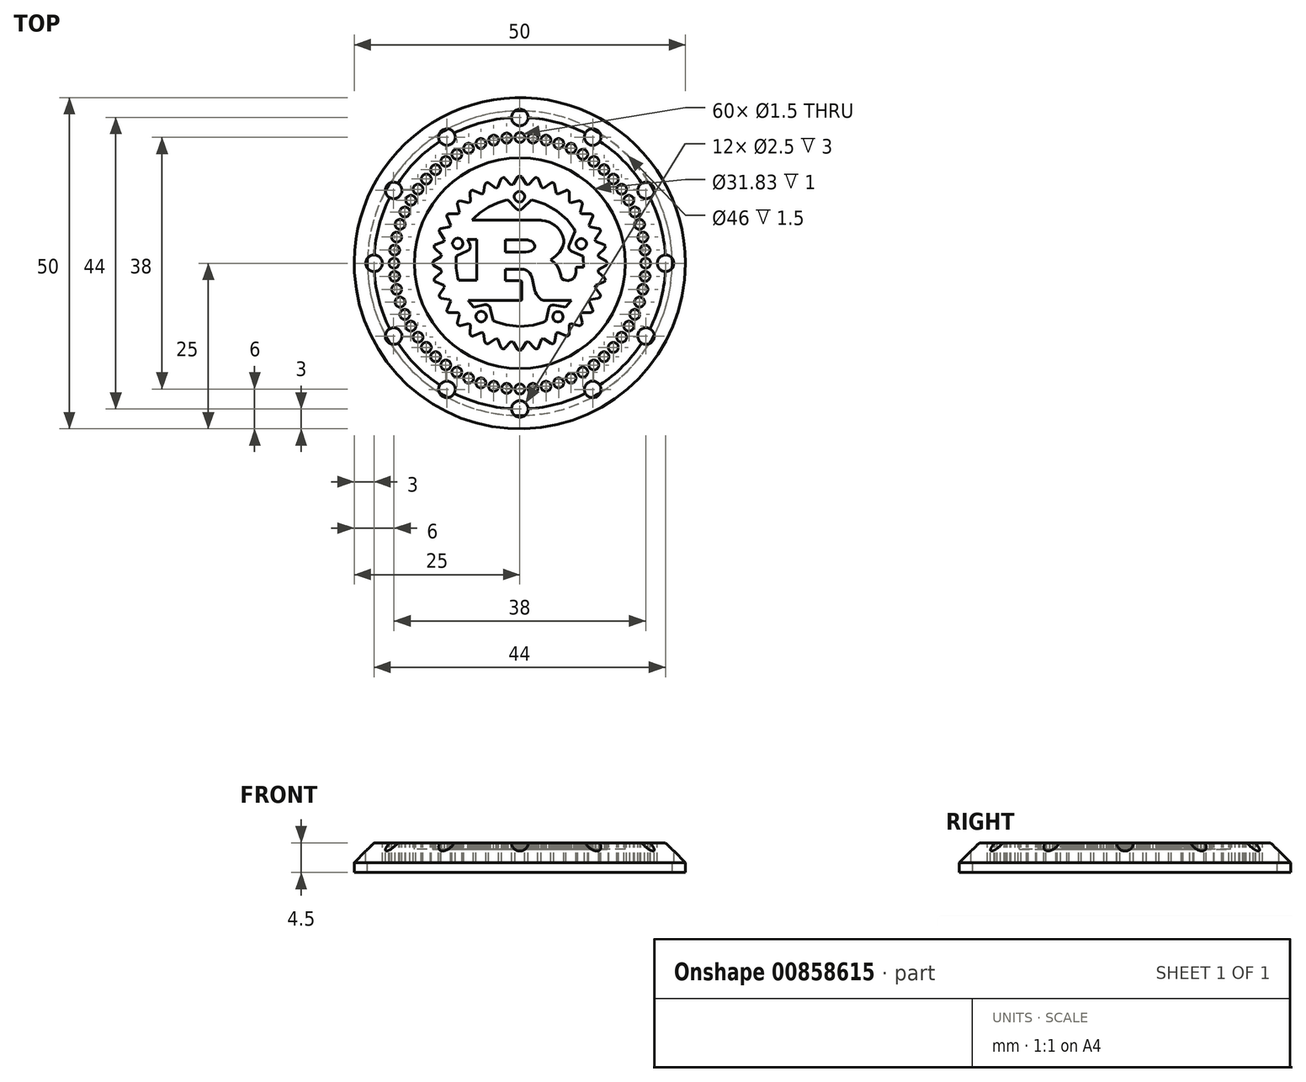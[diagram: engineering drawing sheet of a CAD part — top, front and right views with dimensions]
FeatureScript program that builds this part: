
annotation { "Feature Type Name" : "Feature", "Feature Type Description" : "" }
export const myFeature = defineFeature(function(context is Context, id is Id, definition is map)
    precondition{}
    {
        {
            var Q0;
            Q0=qCreatedBy(makeId("Top.planeOp"),FACE);
            var sketch = newSketch(context, id + "F0", { "sketchPlane" : qUnion([Q0])});
            skCircle(sketch, "E0", {"center": v(0, 0) * mm, "radius": 25 * mm});
            skSolve(sketch);
        }
        {
            var Q0;
            Q0 = qSketchRegion(id + "F0", true);
            extrude(context, id + "F1", {"entities" : qUnion([Q0]), "depth" : 3 * mm, "offsetDistance" : 25 * mm});
        }
        {
            var Q0;
            Q0=makeQuery(id+"F1.opExtrude","CAP_FACE",FACE,{"disambiguationData":[OSD([sQuery(id+"F0.wireOp",EDGE,"E0")])],"isStart":false});
            var sketch = newSketch(context, id + "F2", { "sketchPlane" : qUnion([Q0])});
            skCircle(sketch, "E1", {"center": v(0, 19) * mm, "radius": 0.75 * mm});
            skCircle(sketch, "E2.1.0", {"center": v(-1.99, 18.9) * mm, "radius": 0.75 * mm});
            skCircle(sketch, "E2.2.0", {"center": v(-3.95, 18.58) * mm, "radius": 0.75 * mm});
            skCircle(sketch, "E2.3.0", {"center": v(-5.87, 18.07) * mm, "radius": 0.75 * mm});
            skCircle(sketch, "E2.4.0", {"center": v(-7.73, 17.36) * mm, "radius": 0.75 * mm});
            skCircle(sketch, "E2.5.0", {"center": v(-9.5, 16.45) * mm, "radius": 0.75 * mm});
            skCircle(sketch, "E2.6.0", {"center": v(-11.17, 15.37) * mm, "radius": 0.75 * mm});
            skCircle(sketch, "E2.7.0", {"center": v(-12.71, 14.12) * mm, "radius": 0.75 * mm});
            skCircle(sketch, "E2.8.0", {"center": v(-14.12, 12.71) * mm, "radius": 0.75 * mm});
            skCircle(sketch, "E2.9.0", {"center": v(-15.37, 11.17) * mm, "radius": 0.75 * mm});
            skCircle(sketch, "E2.10.0", {"center": v(-16.45, 9.5) * mm, "radius": 0.75 * mm});
            skCircle(sketch, "E2.11.0", {"center": v(-17.36, 7.73) * mm, "radius": 0.75 * mm});
            skCircle(sketch, "E2.12.0", {"center": v(-18.07, 5.87) * mm, "radius": 0.75 * mm});
            skCircle(sketch, "E2.13.0", {"center": v(-18.58, 3.95) * mm, "radius": 0.75 * mm});
            skCircle(sketch, "E2.14.0", {"center": v(-18.9, 1.99) * mm, "radius": 0.75 * mm});
            skCircle(sketch, "E2.15.0", {"center": v(-19, 0) * mm, "radius": 0.75 * mm});
            skCircle(sketch, "E2.16.0", {"center": v(-18.9, -1.99) * mm, "radius": 0.75 * mm});
            skCircle(sketch, "E2.17.0", {"center": v(-18.58, -3.95) * mm, "radius": 0.75 * mm});
            skCircle(sketch, "E2.18.0", {"center": v(-18.07, -5.87) * mm, "radius": 0.75 * mm});
            skCircle(sketch, "E2.19.0", {"center": v(-17.36, -7.73) * mm, "radius": 0.75 * mm});
            skCircle(sketch, "E2.20.0", {"center": v(-16.45, -9.5) * mm, "radius": 0.75 * mm});
            skCircle(sketch, "E2.21.0", {"center": v(-15.37, -11.17) * mm, "radius": 0.75 * mm});
            skCircle(sketch, "E2.22.0", {"center": v(-14.12, -12.71) * mm, "radius": 0.75 * mm});
            skCircle(sketch, "E2.23.0", {"center": v(-12.71, -14.12) * mm, "radius": 0.75 * mm});
            skCircle(sketch, "E2.24.0", {"center": v(-11.17, -15.37) * mm, "radius": 0.75 * mm});
            skCircle(sketch, "E2.25.0", {"center": v(-9.5, -16.45) * mm, "radius": 0.75 * mm});
            skCircle(sketch, "E2.26.0", {"center": v(-7.73, -17.36) * mm, "radius": 0.75 * mm});
            skCircle(sketch, "E2.27.0", {"center": v(-5.87, -18.07) * mm, "radius": 0.75 * mm});
            skCircle(sketch, "E2.28.0", {"center": v(-3.95, -18.58) * mm, "radius": 0.75 * mm});
            skCircle(sketch, "E2.29.0", {"center": v(-1.99, -18.9) * mm, "radius": 0.75 * mm});
            skPoint(sketch, "E2.center", {"position": v(0, 0) * mm});
            skCircle(sketch, "E3.1.30.0", {"center": v(0, -19) * mm, "radius": 0.75 * mm});
            skCircle(sketch, "E3.1.31.0", {"center": v(1.99, -18.9) * mm, "radius": 0.75 * mm});
            skCircle(sketch, "E3.1.32.0", {"center": v(3.95, -18.58) * mm, "radius": 0.75 * mm});
            skCircle(sketch, "E3.1.33.0", {"center": v(5.87, -18.07) * mm, "radius": 0.75 * mm});
            skCircle(sketch, "E3.1.34.0", {"center": v(7.73, -17.36) * mm, "radius": 0.75 * mm});
            skCircle(sketch, "E3.1.35.0", {"center": v(9.5, -16.45) * mm, "radius": 0.75 * mm});
            skCircle(sketch, "E3.1.36.0", {"center": v(11.17, -15.37) * mm, "radius": 0.75 * mm});
            skCircle(sketch, "E3.1.37.0", {"center": v(12.71, -14.12) * mm, "radius": 0.75 * mm});
            skCircle(sketch, "E3.1.38.0", {"center": v(14.12, -12.71) * mm, "radius": 0.75 * mm});
            skCircle(sketch, "E3.1.39.0", {"center": v(15.37, -11.17) * mm, "radius": 0.75 * mm});
            skCircle(sketch, "E3.1.40.0", {"center": v(16.45, -9.5) * mm, "radius": 0.75 * mm});
            skCircle(sketch, "E3.1.41.0", {"center": v(17.36, -7.73) * mm, "radius": 0.75 * mm});
            skCircle(sketch, "E3.1.42.0", {"center": v(18.07, -5.87) * mm, "radius": 0.75 * mm});
            skCircle(sketch, "E3.1.43.0", {"center": v(18.58, -3.95) * mm, "radius": 0.75 * mm});
            skCircle(sketch, "E3.1.44.0", {"center": v(18.9, -1.99) * mm, "radius": 0.75 * mm});
            skCircle(sketch, "E3.1.45.0", {"center": v(19, 0) * mm, "radius": 0.75 * mm});
            skCircle(sketch, "E3.1.46.0", {"center": v(18.9, 1.99) * mm, "radius": 0.75 * mm});
            skCircle(sketch, "E3.1.47.0", {"center": v(18.58, 3.95) * mm, "radius": 0.75 * mm});
            skCircle(sketch, "E3.1.48.0", {"center": v(18.07, 5.87) * mm, "radius": 0.75 * mm});
            skCircle(sketch, "E3.1.49.0", {"center": v(17.36, 7.73) * mm, "radius": 0.75 * mm});
            skCircle(sketch, "E3.1.50.0", {"center": v(16.45, 9.5) * mm, "radius": 0.75 * mm});
            skCircle(sketch, "E3.1.51.0", {"center": v(15.37, 11.17) * mm, "radius": 0.75 * mm});
            skCircle(sketch, "E3.1.52.0", {"center": v(14.12, 12.71) * mm, "radius": 0.75 * mm});
            skCircle(sketch, "E3.1.53.0", {"center": v(12.71, 14.12) * mm, "radius": 0.75 * mm});
            skCircle(sketch, "E3.1.54.0", {"center": v(11.17, 15.37) * mm, "radius": 0.75 * mm});
            skCircle(sketch, "E3.1.55.0", {"center": v(9.5, 16.45) * mm, "radius": 0.75 * mm});
            skCircle(sketch, "E3.1.56.0", {"center": v(7.73, 17.36) * mm, "radius": 0.75 * mm});
            skCircle(sketch, "E3.1.57.0", {"center": v(5.87, 18.07) * mm, "radius": 0.75 * mm});
            skCircle(sketch, "E3.1.58.0", {"center": v(3.95, 18.58) * mm, "radius": 0.75 * mm});
            skCircle(sketch, "E3.1.59.0", {"center": v(1.99, 18.9) * mm, "radius": 0.75 * mm});
            skSolve(sketch);
        }
        {
            var Q0;
            Q0 = qSketchRegion(id + "F2", true);
            extrude(context, id + "F3", {"entities" : qUnion([Q0]), "operationType" : NewBodyOperationType.REMOVE, "oppositeDirection" : true, "depth" : 3 * mm, "offsetDistance" : 25 * mm});
        }
        {
            var Q0;
            {var subQ66=sQuery(id+"F2.wireOp",EDGE,"E2.1.0");var subQ67=sQuery(id+"F2.wireOp",EDGE,"E1");var subQ68=makeQuery(id+"F2.imprint","INTERSECT",VERTEX,{"disambiguationData":[OD(1.0)],"derivedFrom":[subQ67,subQ66]});Q0=makeQuery(id+"F3.boolean.opBoolean","SPLIT",FACE,{"disambiguationData":[TD([makeQuery(id+"F3.opExtrude","SWEPT_FACE",FACE,{"disambiguationData":[OSD([subQ67]),TDD([makeQuery(id+"F2.imprint","IMPRINT",EDGE,{"disambiguationData":[TD([[subQ68,-1.0]])],"derivedFrom":subQ67})])]})])],"derivedFrom":makeQuery(id+"F1.opExtrude","CAP_FACE",FACE,{"disambiguationData":[OSD([sQuery(id+"F0.wireOp",EDGE,"E0")])],"isStart":false})});}
            var sketch = newSketch(context, id + "F4", { "sketchPlane" : qUnion([Q0])});
            skCircle(sketch, "E4", {"center": v(0, 22) * mm, "radius": 1.25 * mm});
            skCircle(sketch, "E5.1.0", {"center": v(-11, 19.05) * mm, "radius": 1.25 * mm});
            skCircle(sketch, "E5.2.0", {"center": v(-19.05, 11) * mm, "radius": 1.25 * mm});
            skCircle(sketch, "E5.3.0", {"center": v(-22, 0) * mm, "radius": 1.25 * mm});
            skCircle(sketch, "E5.4.0", {"center": v(-19.05, -11) * mm, "radius": 1.25 * mm});
            skCircle(sketch, "E5.5.0", {"center": v(-11, -19.05) * mm, "radius": 1.25 * mm});
            skCircle(sketch, "E5.6.0", {"center": v(0, -22) * mm, "radius": 1.25 * mm});
            skCircle(sketch, "E5.7.0", {"center": v(11, -19.05) * mm, "radius": 1.25 * mm});
            skCircle(sketch, "E5.8.0", {"center": v(19.05, -11) * mm, "radius": 1.25 * mm});
            skCircle(sketch, "E5.9.0", {"center": v(22, 0) * mm, "radius": 1.25 * mm});
            skCircle(sketch, "E5.10.0", {"center": v(19.05, 11) * mm, "radius": 1.25 * mm});
            skCircle(sketch, "E5.11.0", {"center": v(11, 19.05) * mm, "radius": 1.25 * mm});
            skPoint(sketch, "E5.center", {"position": v(0, 0) * mm});
            skSolve(sketch);
        }
        {
            var Q0;
            Q0 = qSketchRegion(id + "F4", true);
            extrude(context, id + "F5", {"entities" : qUnion([Q0]), "operationType" : NewBodyOperationType.REMOVE, "oppositeDirection" : true, "depth" : 3 * mm, "offsetDistance" : 25 * mm});
        }
        {
            var Q0;
            Q0=makeQuery(id+"F1.opExtrude","CAP_EDGE",EDGE,{"disambiguationData":[OSD([sQuery(id+"F0.wireOp",EDGE,"E0")])],"isStart":false});
            chamfer(context, id + "F6", {"entities" : qUnion([Q0]), "width" : 3 * mm, "tangentPropagation" : true});
        }
        {
            var Q0;
            Q0=makeQuery(id+"F1.opExtrude","CAP_FACE",FACE,{"disambiguationData":[OSD([sQuery(id+"F0.wireOp",EDGE,"E0")])],"isStart":false});
            var sketch = newSketch(context, id + "F7", { "sketchPlane" : qUnion([Q0])});
            skCircle(sketch, "E6", {"center": v(0, 0) * mm, "radius": 15.91 * mm});
            skSolve(sketch);
        }
        {
            var Q0;
            Q0 = qSketchRegion(id + "F7", true);
            extrude(context, id + "F8", {"entities" : qUnion([Q0]), "operationType" : NewBodyOperationType.REMOVE, "oppositeDirection" : true, "depth" : 1 * mm, "offsetDistance" : 25 * mm});
        }
        {
            var Q0;
            Q0=makeQuery(id+"F8.boolean.opBoolean","COPY",FACE,{"derivedFrom":makeQuery(id+"F8.opExtrude","CAP_FACE",FACE,{"disambiguationData":[OSD([sQuery(id+"F7.wireOp",EDGE,"E6")])],"isStart":false})});
            var sketch = newSketch(context, id + "F9", { "sketchPlane" : qUnion([Q0])});
            skLineSegment(sketch, "E7", {"start": v(-0.82, 10.05) * mm, "end": v(-0.82, 10.13) * mm});
            skLineSegment(sketch, "E8", {"start": v(-0.82, 10.13) * mm, "end": v(-0.76, 10.36) * mm});
            skLineSegment(sketch, "E9", {"start": v(-0.76, 10.36) * mm, "end": v(-0.6, 10.6) * mm});
            skLineSegment(sketch, "E10", {"start": v(-0.6, 10.6) * mm, "end": v(-0.35, 10.77) * mm});
            skLineSegment(sketch, "E11", {"start": v(-0.35, 10.77) * mm, "end": v(-0.12, 10.84) * mm});
            skLineSegment(sketch, "E12", {"start": v(-0.12, 10.84) * mm, "end": v(-0.04, 10.84) * mm});
            skLineSegment(sketch, "E13", {"start": v(-0.04, 10.84) * mm, "end": v(0.03, 10.84) * mm});
            skLineSegment(sketch, "E14", {"start": v(0.03, 10.84) * mm, "end": v(0.26, 10.77) * mm});
            skLineSegment(sketch, "E15", {"start": v(0.26, 10.77) * mm, "end": v(0.51, 10.6) * mm});
            skLineSegment(sketch, "E16", {"start": v(0.51, 10.6) * mm, "end": v(0.68, 10.36) * mm});
            skLineSegment(sketch, "E17", {"start": v(0.68, 10.36) * mm, "end": v(0.74, 10.13) * mm});
            skLineSegment(sketch, "E18", {"start": v(0.74, 10.13) * mm, "end": v(0.74, 10.05) * mm});
            skLineSegment(sketch, "E19", {"start": v(0.74, 10.05) * mm, "end": v(0.74, 9.98) * mm});
            skLineSegment(sketch, "E20", {"start": v(0.74, 9.98) * mm, "end": v(0.68, 9.75) * mm});
            skLineSegment(sketch, "E21", {"start": v(0.68, 9.75) * mm, "end": v(0.51, 9.5) * mm});
            skLineSegment(sketch, "E22", {"start": v(0.51, 9.5) * mm, "end": v(0.26, 9.33) * mm});
            skLineSegment(sketch, "E23", {"start": v(0.26, 9.33) * mm, "end": v(0.03, 9.27) * mm});
            skLineSegment(sketch, "E24", {"start": v(0.03, 9.27) * mm, "end": v(-0.04, 9.27) * mm});
            skLineSegment(sketch, "E25", {"start": v(-0.04, 9.27) * mm, "end": v(-0.12, 9.27) * mm});
            skLineSegment(sketch, "E26", {"start": v(-0.12, 9.27) * mm, "end": v(-0.35, 9.33) * mm});
            skLineSegment(sketch, "E27", {"start": v(-0.35, 9.33) * mm, "end": v(-0.6, 9.5) * mm});
            skLineSegment(sketch, "E28", {"start": v(-0.6, 9.5) * mm, "end": v(-0.76, 9.75) * mm});
            skLineSegment(sketch, "E29", {"start": v(-0.76, 9.75) * mm, "end": v(-0.82, 9.98) * mm});
            skLineSegment(sketch, "E30", {"start": v(-0.82, 9.98) * mm, "end": v(-0.82, 10.05) * mm});
            skLineSegment(sketch, "E31", {"start": v(-10.15, 2.97) * mm, "end": v(-10.15, 3.05) * mm});
            skLineSegment(sketch, "E32", {"start": v(-10.15, 3.05) * mm, "end": v(-10.09, 3.28) * mm});
            skLineSegment(sketch, "E33", {"start": v(-10.09, 3.28) * mm, "end": v(-9.92, 3.53) * mm});
            skLineSegment(sketch, "E34", {"start": v(-9.92, 3.53) * mm, "end": v(-9.67, 3.7) * mm});
            skLineSegment(sketch, "E35", {"start": v(-9.67, 3.7) * mm, "end": v(-9.45, 3.76) * mm});
            skLineSegment(sketch, "E36", {"start": v(-9.45, 3.76) * mm, "end": v(-9.37, 3.76) * mm});
            skLineSegment(sketch, "E37", {"start": v(-9.37, 3.76) * mm, "end": v(-9.3, 3.76) * mm});
            skLineSegment(sketch, "E38", {"start": v(-9.3, 3.76) * mm, "end": v(-9.07, 3.7) * mm});
            skLineSegment(sketch, "E39", {"start": v(-9.07, 3.7) * mm, "end": v(-8.82, 3.53) * mm});
            skLineSegment(sketch, "E40", {"start": v(-8.82, 3.53) * mm, "end": v(-8.65, 3.28) * mm});
            skLineSegment(sketch, "E41", {"start": v(-8.65, 3.28) * mm, "end": v(-8.59, 3.05) * mm});
            skLineSegment(sketch, "E42", {"start": v(-8.59, 3.05) * mm, "end": v(-8.59, 2.97) * mm});
            skLineSegment(sketch, "E43", {"start": v(-8.59, 2.97) * mm, "end": v(-8.59, 2.9) * mm});
            skLineSegment(sketch, "E44", {"start": v(-8.59, 2.9) * mm, "end": v(-8.65, 2.67) * mm});
            skLineSegment(sketch, "E45", {"start": v(-8.65, 2.67) * mm, "end": v(-8.82, 2.42) * mm});
            skLineSegment(sketch, "E46", {"start": v(-8.82, 2.42) * mm, "end": v(-9.07, 2.25) * mm});
            skLineSegment(sketch, "E47", {"start": v(-9.07, 2.25) * mm, "end": v(-9.3, 2.2) * mm});
            skLineSegment(sketch, "E48", {"start": v(-9.3, 2.2) * mm, "end": v(-9.37, 2.2) * mm});
            skLineSegment(sketch, "E49", {"start": v(-9.37, 2.2) * mm, "end": v(-9.45, 2.2) * mm});
            skLineSegment(sketch, "E50", {"start": v(-9.45, 2.2) * mm, "end": v(-9.67, 2.25) * mm});
            skLineSegment(sketch, "E51", {"start": v(-9.67, 2.25) * mm, "end": v(-9.92, 2.42) * mm});
            skLineSegment(sketch, "E52", {"start": v(-9.92, 2.42) * mm, "end": v(-10.09, 2.67) * mm});
            skLineSegment(sketch, "E53", {"start": v(-10.09, 2.67) * mm, "end": v(-10.15, 2.9) * mm});
            skLineSegment(sketch, "E54", {"start": v(-10.15, 2.9) * mm, "end": v(-10.15, 2.97) * mm});
            skLineSegment(sketch, "E55", {"start": v(8.5, 2.94) * mm, "end": v(8.5, 3.01) * mm});
            skLineSegment(sketch, "E56", {"start": v(8.5, 3.01) * mm, "end": v(8.57, 3.24) * mm});
            skLineSegment(sketch, "E57", {"start": v(8.57, 3.24) * mm, "end": v(8.73, 3.5) * mm});
            skLineSegment(sketch, "E58", {"start": v(8.73, 3.5) * mm, "end": v(8.98, 3.66) * mm});
            skLineSegment(sketch, "E59", {"start": v(8.98, 3.66) * mm, "end": v(9.21, 3.72) * mm});
            skLineSegment(sketch, "E60", {"start": v(9.21, 3.72) * mm, "end": v(9.29, 3.72) * mm});
            skLineSegment(sketch, "E61", {"start": v(9.29, 3.72) * mm, "end": v(9.36, 3.72) * mm});
            skLineSegment(sketch, "E62", {"start": v(9.36, 3.72) * mm, "end": v(9.6, 3.66) * mm});
            skLineSegment(sketch, "E63", {"start": v(9.6, 3.66) * mm, "end": v(9.84, 3.5) * mm});
            skLineSegment(sketch, "E64", {"start": v(9.84, 3.5) * mm, "end": v(10, 3.24) * mm});
            skLineSegment(sketch, "E65", {"start": v(10, 3.24) * mm, "end": v(10.07, 3.01) * mm});
            skLineSegment(sketch, "E66", {"start": v(10.07, 3.01) * mm, "end": v(10.07, 2.94) * mm});
            skLineSegment(sketch, "E67", {"start": v(10.07, 2.94) * mm, "end": v(10.07, 2.86) * mm});
            skLineSegment(sketch, "E68", {"start": v(10.07, 2.86) * mm, "end": v(10, 2.63) * mm});
            skLineSegment(sketch, "E69", {"start": v(10, 2.63) * mm, "end": v(9.84, 2.39) * mm});
            skLineSegment(sketch, "E70", {"start": v(9.84, 2.39) * mm, "end": v(9.6, 2.22) * mm});
            skLineSegment(sketch, "E71", {"start": v(9.6, 2.22) * mm, "end": v(9.36, 2.16) * mm});
            skLineSegment(sketch, "E72", {"start": v(9.36, 2.16) * mm, "end": v(9.29, 2.16) * mm});
            skLineSegment(sketch, "E73", {"start": v(9.29, 2.16) * mm, "end": v(9.21, 2.16) * mm});
            skLineSegment(sketch, "E74", {"start": v(9.21, 2.16) * mm, "end": v(8.98, 2.22) * mm});
            skLineSegment(sketch, "E75", {"start": v(8.98, 2.22) * mm, "end": v(8.73, 2.39) * mm});
            skLineSegment(sketch, "E76", {"start": v(8.73, 2.39) * mm, "end": v(8.57, 2.63) * mm});
            skLineSegment(sketch, "E77", {"start": v(8.57, 2.63) * mm, "end": v(8.5, 2.86) * mm});
            skLineSegment(sketch, "E78", {"start": v(8.5, 2.86) * mm, "end": v(8.5, 2.94) * mm});
            skLineSegment(sketch, "E79", {"start": v(-7.89, 1.87) * mm, "end": v(-7.82, 1.9) * mm});
            skLineSegment(sketch, "E80", {"start": v(-7.82, 1.9) * mm, "end": v(-7.66, 2.03) * mm});
            skLineSegment(sketch, "E81", {"start": v(-7.66, 2.03) * mm, "end": v(-7.51, 2.26) * mm});
            skLineSegment(sketch, "E82", {"start": v(-7.51, 2.26) * mm, "end": v(-7.46, 2.53) * mm});
            skLineSegment(sketch, "E83", {"start": v(-7.46, 2.53) * mm, "end": v(-7.5, 2.75) * mm});
            skLineSegment(sketch, "E84", {"start": v(-7.5, 2.75) * mm, "end": v(-7.53, 2.8) * mm});
            skLineSegment(sketch, "E85", {"start": v(-7.53, 2.8) * mm, "end": v(-7.87, 3.6) * mm});
            skLineSegment(sketch, "E86", {"start": v(-7.87, 3.6) * mm, "end": v(-6.5, 3.6) * mm});
            skLineSegment(sketch, "E87", {"start": v(-6.5, 3.6) * mm, "end": v(-6.5, -2.56) * mm});
            skLineSegment(sketch, "E88", {"start": v(-6.5, -2.56) * mm, "end": v(-9.26, -2.56) * mm});
            skLineSegment(sketch, "E89", {"start": v(-9.26, -2.56) * mm, "end": v(-9.35, -2.26) * mm});
            skLineSegment(sketch, "E90", {"start": v(-9.35, -2.26) * mm, "end": v(-9.6, -0.73) * mm});
            skLineSegment(sketch, "E91", {"start": v(-9.6, -0.73) * mm, "end": v(-9.6, 0.8) * mm});
            skLineSegment(sketch, "E92", {"start": v(-9.6, 0.8) * mm, "end": v(-9.57, 1.12) * mm});
            skLineSegment(sketch, "E93", {"start": v(-9.57, 1.12) * mm, "end": v(-7.89, 1.87) * mm});
            skLineSegment(sketch, "E94", {"start": v(-2.18, 1.72) * mm, "end": v(-2.18, 3.53) * mm});
            skLineSegment(sketch, "E95", {"start": v(-2.18, 3.53) * mm, "end": v(1.07, 3.53) * mm});
            skLineSegment(sketch, "E96", {"start": v(1.07, 3.53) * mm, "end": v(1.1, 3.53) * mm});
            skLineSegment(sketch, "E97", {"start": v(1.1, 3.53) * mm, "end": v(1.17, 3.52) * mm});
            skLineSegment(sketch, "E98", {"start": v(1.17, 3.52) * mm, "end": v(1.32, 3.49) * mm});
            skLineSegment(sketch, "E99", {"start": v(1.32, 3.49) * mm, "end": v(1.52, 3.43) * mm});
            skLineSegment(sketch, "E100", {"start": v(1.52, 3.43) * mm, "end": v(1.72, 3.34) * mm});
            skLineSegment(sketch, "E101", {"start": v(1.72, 3.34) * mm, "end": v(1.92, 3.21) * mm});
            skLineSegment(sketch, "E102", {"start": v(1.92, 3.21) * mm, "end": v(2.1, 3.04) * mm});
            skLineSegment(sketch, "E103", {"start": v(2.1, 3.04) * mm, "end": v(2.2, 2.83) * mm});
            skLineSegment(sketch, "E104", {"start": v(2.2, 2.83) * mm, "end": v(2.25, 2.64) * mm});
            skLineSegment(sketch, "E105", {"start": v(2.25, 2.64) * mm, "end": v(2.25, 2.57) * mm});
            skLineSegment(sketch, "E106", {"start": v(2.25, 2.57) * mm, "end": v(2.25, 2.47) * mm});
            skLineSegment(sketch, "E107", {"start": v(2.25, 2.47) * mm, "end": v(2.12, 2.17) * mm});
            skLineSegment(sketch, "E108", {"start": v(2.12, 2.17) * mm, "end": v(1.78, 1.9) * mm});
            skLineSegment(sketch, "E109", {"start": v(1.78, 1.9) * mm, "end": v(1.32, 1.76) * mm});
            skLineSegment(sketch, "E110", {"start": v(1.32, 1.76) * mm, "end": v(0.96, 1.72) * mm});
            skLineSegment(sketch, "E111", {"start": v(0.96, 1.72) * mm, "end": v(0.83, 1.72) * mm});
            skLineSegment(sketch, "E112", {"start": v(0.83, 1.72) * mm, "end": v(-2.18, 1.72) * mm});
            skLineSegment(sketch, "E113", {"start": v(-6.62, -8.04) * mm, "end": v(-6.62, -7.97) * mm});
            skLineSegment(sketch, "E114", {"start": v(-6.62, -7.97) * mm, "end": v(-6.56, -7.75) * mm});
            skLineSegment(sketch, "E115", {"start": v(-6.56, -7.75) * mm, "end": v(-6.42, -7.53) * mm});
            skLineSegment(sketch, "E116", {"start": v(-6.42, -7.53) * mm, "end": v(-6.39, -7.5) * mm});
            skLineSegment(sketch, "E117", {"start": v(-6.39, -7.5) * mm, "end": v(-6.35, -7.45) * mm});
            skLineSegment(sketch, "E118", {"start": v(-6.35, -7.45) * mm, "end": v(-6.13, -7.32) * mm});
            skLineSegment(sketch, "E119", {"start": v(-6.13, -7.32) * mm, "end": v(-5.9, -7.26) * mm});
            skLineSegment(sketch, "E120", {"start": v(-5.9, -7.26) * mm, "end": v(-5.83, -7.26) * mm});
            skLineSegment(sketch, "E121", {"start": v(-5.83, -7.26) * mm, "end": v(-5.76, -7.26) * mm});
            skLineSegment(sketch, "E122", {"start": v(-5.76, -7.26) * mm, "end": v(-5.54, -7.32) * mm});
            skLineSegment(sketch, "E123", {"start": v(-5.54, -7.32) * mm, "end": v(-5.32, -7.45) * mm});
            skLineSegment(sketch, "E124", {"start": v(-5.32, -7.45) * mm, "end": v(-5.28, -7.5) * mm});
            skLineSegment(sketch, "E125", {"start": v(-5.28, -7.5) * mm, "end": v(-5.24, -7.53) * mm});
            skLineSegment(sketch, "E126", {"start": v(-5.24, -7.53) * mm, "end": v(-5.11, -7.75) * mm});
            skLineSegment(sketch, "E127", {"start": v(-5.11, -7.75) * mm, "end": v(-5.05, -7.97) * mm});
            skLineSegment(sketch, "E128", {"start": v(-5.05, -7.97) * mm, "end": v(-5.05, -8.04) * mm});
            skLineSegment(sketch, "E129", {"start": v(-5.05, -8.04) * mm, "end": v(-5.05, -8.12) * mm});
            skLineSegment(sketch, "E130", {"start": v(-5.05, -8.12) * mm, "end": v(-5.11, -8.35) * mm});
            skLineSegment(sketch, "E131", {"start": v(-5.11, -8.35) * mm, "end": v(-5.28, -8.6) * mm});
            skLineSegment(sketch, "E132", {"start": v(-5.28, -8.6) * mm, "end": v(-5.53, -8.76) * mm});
            skLineSegment(sketch, "E133", {"start": v(-5.53, -8.76) * mm, "end": v(-5.76, -8.83) * mm});
            skLineSegment(sketch, "E134", {"start": v(-5.76, -8.83) * mm, "end": v(-5.83, -8.83) * mm});
            skLineSegment(sketch, "E135", {"start": v(-5.83, -8.83) * mm, "end": v(-5.91, -8.83) * mm});
            skLineSegment(sketch, "E136", {"start": v(-5.91, -8.83) * mm, "end": v(-6.14, -8.76) * mm});
            skLineSegment(sketch, "E137", {"start": v(-6.14, -8.76) * mm, "end": v(-6.39, -8.6) * mm});
            skLineSegment(sketch, "E138", {"start": v(-6.39, -8.6) * mm, "end": v(-6.55, -8.35) * mm});
            skLineSegment(sketch, "E139", {"start": v(-6.55, -8.35) * mm, "end": v(-6.62, -8.12) * mm});
            skLineSegment(sketch, "E140", {"start": v(-6.62, -8.12) * mm, "end": v(-6.62, -8.04) * mm});
            skLineSegment(sketch, "E141", {"start": v(4.97, -8.08) * mm, "end": v(4.97, -8) * mm});
            skLineSegment(sketch, "E142", {"start": v(4.97, -8) * mm, "end": v(5.03, -7.78) * mm});
            skLineSegment(sketch, "E143", {"start": v(5.03, -7.78) * mm, "end": v(5.2, -7.53) * mm});
            skLineSegment(sketch, "E144", {"start": v(5.2, -7.53) * mm, "end": v(5.45, -7.36) * mm});
            skLineSegment(sketch, "E145", {"start": v(5.45, -7.36) * mm, "end": v(5.68, -7.3) * mm});
            skLineSegment(sketch, "E146", {"start": v(5.68, -7.3) * mm, "end": v(5.75, -7.3) * mm});
            skLineSegment(sketch, "E147", {"start": v(5.75, -7.3) * mm, "end": v(5.83, -7.3) * mm});
            skLineSegment(sketch, "E148", {"start": v(5.83, -7.3) * mm, "end": v(6.06, -7.36) * mm});
            skLineSegment(sketch, "E149", {"start": v(6.06, -7.36) * mm, "end": v(6.3, -7.53) * mm});
            skLineSegment(sketch, "E150", {"start": v(6.3, -7.53) * mm, "end": v(6.47, -7.78) * mm});
            skLineSegment(sketch, "E151", {"start": v(6.47, -7.78) * mm, "end": v(6.53, -8) * mm});
            skLineSegment(sketch, "E152", {"start": v(6.53, -8) * mm, "end": v(6.53, -8.08) * mm});
            skLineSegment(sketch, "E153", {"start": v(6.53, -8.08) * mm, "end": v(6.53, -8.16) * mm});
            skLineSegment(sketch, "E154", {"start": v(6.53, -8.16) * mm, "end": v(6.47, -8.38) * mm});
            skLineSegment(sketch, "E155", {"start": v(6.47, -8.38) * mm, "end": v(6.3, -8.63) * mm});
            skLineSegment(sketch, "E156", {"start": v(6.3, -8.63) * mm, "end": v(6.06, -8.8) * mm});
            skLineSegment(sketch, "E157", {"start": v(6.06, -8.8) * mm, "end": v(5.83, -8.86) * mm});
            skLineSegment(sketch, "E158", {"start": v(5.83, -8.86) * mm, "end": v(5.75, -8.86) * mm});
            skLineSegment(sketch, "E159", {"start": v(5.75, -8.86) * mm, "end": v(5.68, -8.86) * mm});
            skLineSegment(sketch, "E160", {"start": v(5.68, -8.86) * mm, "end": v(5.45, -8.8) * mm});
            skLineSegment(sketch, "E161", {"start": v(5.45, -8.8) * mm, "end": v(5.2, -8.63) * mm});
            skLineSegment(sketch, "E162", {"start": v(5.2, -8.63) * mm, "end": v(5.03, -8.38) * mm});
            skLineSegment(sketch, "E163", {"start": v(5.03, -8.38) * mm, "end": v(4.97, -8.16) * mm});
            skLineSegment(sketch, "E164", {"start": v(4.97, -8.16) * mm, "end": v(4.97, -8.08) * mm});
            skLineSegment(sketch, "E165", {"start": v(5.21, -6.3) * mm, "end": v(5.14, -6.3) * mm});
            skLineSegment(sketch, "E166", {"start": v(5.14, -6.3) * mm, "end": v(4.93, -6.3) * mm});
            skLineSegment(sketch, "E167", {"start": v(4.93, -6.3) * mm, "end": v(4.67, -6.4) * mm});
            skLineSegment(sketch, "E168", {"start": v(4.67, -6.4) * mm, "end": v(4.48, -6.6) * mm});
            skLineSegment(sketch, "E169", {"start": v(4.48, -6.6) * mm, "end": v(4.38, -6.79) * mm});
            skLineSegment(sketch, "E170", {"start": v(4.38, -6.79) * mm, "end": v(4.36, -6.86) * mm});
            skLineSegment(sketch, "E171", {"start": v(4.36, -6.86) * mm, "end": v(3.97, -8.69) * mm});
            skLineSegment(sketch, "E172", {"start": v(3.97, -8.69) * mm, "end": v(3.5, -8.9) * mm});
            skLineSegment(sketch, "E173", {"start": v(3.5, -8.9) * mm, "end": v(2, -9.34) * mm});
            skLineSegment(sketch, "E174", {"start": v(2, -9.34) * mm, "end": v(-0.05, -9.55) * mm});
            skLineSegment(sketch, "E175", {"start": v(-0.05, -9.55) * mm, "end": v(-2.09, -9.32) * mm});
            skLineSegment(sketch, "E176", {"start": v(-2.09, -9.32) * mm, "end": v(-3.59, -8.87) * mm});
            skLineSegment(sketch, "E177", {"start": v(-3.59, -8.87) * mm, "end": v(-4.06, -8.65) * mm});
            skLineSegment(sketch, "E178", {"start": v(-4.06, -8.65) * mm, "end": v(-4.45, -6.82) * mm});
            skLineSegment(sketch, "E179", {"start": v(-4.45, -6.82) * mm, "end": v(-4.46, -6.75) * mm});
            skLineSegment(sketch, "E180", {"start": v(-4.46, -6.75) * mm, "end": v(-4.56, -6.56) * mm});
            skLineSegment(sketch, "E181", {"start": v(-4.56, -6.56) * mm, "end": v(-4.76, -6.37) * mm});
            skLineSegment(sketch, "E182", {"start": v(-4.76, -6.37) * mm, "end": v(-5.01, -6.27) * mm});
            skLineSegment(sketch, "E183", {"start": v(-5.01, -6.27) * mm, "end": v(-5.23, -6.25) * mm});
            skLineSegment(sketch, "E184", {"start": v(-5.23, -6.25) * mm, "end": v(-5.3, -6.27) * mm});
            skLineSegment(sketch, "E185", {"start": v(-5.3, -6.27) * mm, "end": v(-6.91, -6.62) * mm});
            skLineSegment(sketch, "E186", {"start": v(-6.91, -6.62) * mm, "end": v(-6.99, -6.54) * mm});
            skLineSegment(sketch, "E187", {"start": v(-6.99, -6.54) * mm, "end": v(-7.68, -5.72) * mm});
            skLineSegment(sketch, "E188", {"start": v(-7.68, -5.72) * mm, "end": v(-7.75, -5.63) * mm});
            skLineSegment(sketch, "E189", {"start": v(-7.75, -5.63) * mm, "end": v(0.12, -5.63) * mm});
            skLineSegment(sketch, "E190", {"start": v(0.12, -5.63) * mm, "end": v(0.15, -5.63) * mm});
            skLineSegment(sketch, "E191", {"start": v(0.15, -5.63) * mm, "end": v(0.23, -5.61) * mm});
            skLineSegment(sketch, "E192", {"start": v(0.23, -5.61) * mm, "end": v(0.27, -5.55) * mm});
            skLineSegment(sketch, "E193", {"start": v(0.27, -5.55) * mm, "end": v(0.27, -5.53) * mm});
            skLineSegment(sketch, "E194", {"start": v(0.27, -5.53) * mm, "end": v(0.27, -2.75) * mm});
            skLineSegment(sketch, "E195", {"start": v(0.27, -2.75) * mm, "end": v(0.27, -2.73) * mm});
            skLineSegment(sketch, "E196", {"start": v(0.27, -2.73) * mm, "end": v(0.23, -2.67) * mm});
            skLineSegment(sketch, "E197", {"start": v(0.23, -2.67) * mm, "end": v(0.15, -2.65) * mm});
            skLineSegment(sketch, "E198", {"start": v(0.15, -2.65) * mm, "end": v(0.12, -2.65) * mm});
            skLineSegment(sketch, "E199", {"start": v(0.12, -2.65) * mm, "end": v(-2.18, -2.65) * mm});
            skLineSegment(sketch, "E200", {"start": v(-2.18, -2.65) * mm, "end": v(-2.18, -0.89) * mm});
            skLineSegment(sketch, "E201", {"start": v(-2.18, -0.89) * mm, "end": v(0.3, -0.89) * mm});
            skLineSegment(sketch, "E202", {"start": v(0.3, -0.89) * mm, "end": v(0.34, -0.89) * mm});
            skLineSegment(sketch, "E203", {"start": v(0.34, -0.89) * mm, "end": v(0.43, -0.9) * mm});
            skLineSegment(sketch, "E204", {"start": v(0.43, -0.9) * mm, "end": v(0.6, -0.92) * mm});
            skLineSegment(sketch, "E205", {"start": v(0.6, -0.92) * mm, "end": v(0.8, -0.98) * mm});
            skLineSegment(sketch, "E206", {"start": v(0.8, -0.98) * mm, "end": v(1.04, -1.08) * mm});
            skLineSegment(sketch, "E207", {"start": v(1.04, -1.08) * mm, "end": v(1.28, -1.24) * mm});
            skLineSegment(sketch, "E208", {"start": v(1.28, -1.24) * mm, "end": v(1.5, -1.48) * mm});
            skLineSegment(sketch, "E209", {"start": v(1.5, -1.48) * mm, "end": v(1.7, -1.8) * mm});
            skLineSegment(sketch, "E210", {"start": v(1.7, -1.8) * mm, "end": v(1.81, -2.1) * mm});
            skLineSegment(sketch, "E211", {"start": v(1.81, -2.1) * mm, "end": v(1.84, -2.22) * mm});
            skLineSegment(sketch, "E212", {"start": v(1.84, -2.22) * mm, "end": v(1.86, -2.31) * mm});
            skLineSegment(sketch, "E213", {"start": v(1.86, -2.31) * mm, "end": v(1.93, -2.64) * mm});
            skLineSegment(sketch, "E214", {"start": v(1.93, -2.64) * mm, "end": v(2.05, -3.24) * mm});
            skLineSegment(sketch, "E215", {"start": v(2.05, -3.24) * mm, "end": v(2.18, -3.83) * mm});
            skLineSegment(sketch, "E216", {"start": v(2.18, -3.83) * mm, "end": v(2.27, -4.17) * mm});
            skLineSegment(sketch, "E217", {"start": v(2.27, -4.17) * mm, "end": v(2.3, -4.27) * mm});
            skLineSegment(sketch, "E218", {"start": v(2.3, -4.27) * mm, "end": v(2.34, -4.38) * mm});
            skLineSegment(sketch, "E219", {"start": v(2.34, -4.38) * mm, "end": v(2.5, -4.68) * mm});
            skLineSegment(sketch, "E220", {"start": v(2.5, -4.68) * mm, "end": v(2.81, -5.12) * mm});
            skLineSegment(sketch, "E221", {"start": v(2.81, -5.12) * mm, "end": v(3.23, -5.48) * mm});
            skLineSegment(sketch, "E222", {"start": v(3.23, -5.48) * mm, "end": v(3.58, -5.63) * mm});
            skLineSegment(sketch, "E223", {"start": v(3.58, -5.63) * mm, "end": v(3.7, -5.63) * mm});
            skLineSegment(sketch, "E224", {"start": v(3.7, -5.63) * mm, "end": v(7.76, -5.63) * mm});
            skLineSegment(sketch, "E225", {"start": v(7.76, -5.63) * mm, "end": v(7.69, -5.72) * mm});
            skLineSegment(sketch, "E226", {"start": v(7.69, -5.72) * mm, "end": v(6.95, -6.58) * mm});
            skLineSegment(sketch, "E227", {"start": v(6.95, -6.58) * mm, "end": v(6.87, -6.66) * mm});
            skLineSegment(sketch, "E228", {"start": v(6.87, -6.66) * mm, "end": v(5.21, -6.3) * mm});
            skLineSegment(sketch, "E229", {"start": v(9.58, 1.04) * mm, "end": v(9.6, 0.9) * mm});
            skLineSegment(sketch, "E230", {"start": v(9.6, 0.9) * mm, "end": v(9.61, -0.5) * mm});
            skLineSegment(sketch, "E231", {"start": v(9.61, -0.5) * mm, "end": v(9.6, -0.63) * mm});
            skLineSegment(sketch, "E232", {"start": v(9.6, -0.63) * mm, "end": v(8.61, -0.63) * mm});
            skLineSegment(sketch, "E233", {"start": v(8.61, -0.63) * mm, "end": v(8.59, -0.63) * mm});
            skLineSegment(sketch, "E234", {"start": v(8.59, -0.63) * mm, "end": v(8.5, -0.67) * mm});
            skLineSegment(sketch, "E235", {"start": v(8.5, -0.67) * mm, "end": v(8.47, -0.76) * mm});
            skLineSegment(sketch, "E236", {"start": v(8.47, -0.76) * mm, "end": v(8.47, -0.8) * mm});
            skLineSegment(sketch, "E237", {"start": v(8.47, -0.8) * mm, "end": v(8.47, -1.25) * mm});
            skLineSegment(sketch, "E238", {"start": v(8.47, -1.25) * mm, "end": v(8.47, -1.4) * mm});
            skLineSegment(sketch, "E239", {"start": v(8.47, -1.4) * mm, "end": v(8.37, -1.9) * mm});
            skLineSegment(sketch, "E240", {"start": v(8.37, -1.9) * mm, "end": v(8.1, -2.3) * mm});
            skLineSegment(sketch, "E241", {"start": v(8.1, -2.3) * mm, "end": v(7.74, -2.52) * mm});
            skLineSegment(sketch, "E242", {"start": v(7.74, -2.52) * mm, "end": v(7.45, -2.6) * mm});
            skLineSegment(sketch, "E243", {"start": v(7.45, -2.6) * mm, "end": v(7.35, -2.6) * mm});
            skLineSegment(sketch, "E244", {"start": v(7.35, -2.6) * mm, "end": v(7.25, -2.62) * mm});
            skLineSegment(sketch, "E245", {"start": v(7.25, -2.62) * mm, "end": v(6.97, -2.6) * mm});
            skLineSegment(sketch, "E246", {"start": v(6.97, -2.6) * mm, "end": v(6.62, -2.48) * mm});
            skLineSegment(sketch, "E247", {"start": v(6.62, -2.48) * mm, "end": v(6.35, -2.3) * mm});
            skLineSegment(sketch, "E248", {"start": v(6.35, -2.3) * mm, "end": v(6.23, -2.15) * mm});
            skLineSegment(sketch, "E249", {"start": v(6.23, -2.15) * mm, "end": v(6.22, -2.09) * mm});
            skLineSegment(sketch, "E250", {"start": v(6.22, -2.09) * mm, "end": v(6.17, -1.83) * mm});
            skLineSegment(sketch, "E251", {"start": v(6.17, -1.83) * mm, "end": v(5.96, -1.06) * mm});
            skLineSegment(sketch, "E252", {"start": v(5.96, -1.06) * mm, "end": v(5.61, -0.37) * mm});
            skLineSegment(sketch, "E253", {"start": v(5.61, -0.37) * mm, "end": v(5.18, 0.11) * mm});
            skLineSegment(sketch, "E254", {"start": v(5.18, 0.11) * mm, "end": v(4.78, 0.44) * mm});
            skLineSegment(sketch, "E255", {"start": v(4.78, 0.44) * mm, "end": v(4.65, 0.55) * mm});
            skLineSegment(sketch, "E256", {"start": v(4.65, 0.55) * mm, "end": v(4.83, 0.67) * mm});
            skLineSegment(sketch, "E257", {"start": v(4.83, 0.67) * mm, "end": v(5.36, 1.07) * mm});
            skLineSegment(sketch, "E258", {"start": v(5.36, 1.07) * mm, "end": v(6, 1.7) * mm});
            skLineSegment(sketch, "E259", {"start": v(6, 1.7) * mm, "end": v(6.45, 2.43) * mm});
            skLineSegment(sketch, "E260", {"start": v(6.45, 2.43) * mm, "end": v(6.62, 3.07) * mm});
            skLineSegment(sketch, "E261", {"start": v(6.62, 3.07) * mm, "end": v(6.62, 3.29) * mm});
            skLineSegment(sketch, "E262", {"start": v(6.62, 3.29) * mm, "end": v(6.62, 3.5) * mm});
            skLineSegment(sketch, "E263", {"start": v(6.62, 3.5) * mm, "end": v(6.47, 4.18) * mm});
            skLineSegment(sketch, "E264", {"start": v(6.47, 4.18) * mm, "end": v(6.1, 4.9) * mm});
            skLineSegment(sketch, "E265", {"start": v(6.1, 4.9) * mm, "end": v(5.6, 5.44) * mm});
            skLineSegment(sketch, "E266", {"start": v(5.6, 5.44) * mm, "end": v(5.24, 5.74) * mm});
            skLineSegment(sketch, "E267", {"start": v(5.24, 5.74) * mm, "end": v(5.11, 5.83) * mm});
            skLineSegment(sketch, "E268", {"start": v(5.11, 5.83) * mm, "end": v(4.96, 5.93) * mm});
            skLineSegment(sketch, "E269", {"start": v(4.96, 5.93) * mm, "end": v(4.46, 6.17) * mm});
            skLineSegment(sketch, "E270", {"start": v(4.46, 6.17) * mm, "end": v(3.85, 6.38) * mm});
            skLineSegment(sketch, "E271", {"start": v(3.85, 6.38) * mm, "end": v(3.35, 6.48) * mm});
            skLineSegment(sketch, "E272", {"start": v(3.35, 6.48) * mm, "end": v(3.12, 6.5) * mm});
            skLineSegment(sketch, "E273", {"start": v(3.12, 6.5) * mm, "end": v(3.04, 6.5) * mm});
            skLineSegment(sketch, "E274", {"start": v(3.04, 6.5) * mm, "end": v(-7.17, 6.5) * mm});
            skLineSegment(sketch, "E275", {"start": v(-7.17, 6.5) * mm, "end": v(-6.9, 6.8) * mm});
            skLineSegment(sketch, "E276", {"start": v(-6.9, 6.8) * mm, "end": v(-6.03, 7.6) * mm});
            skLineSegment(sketch, "E277", {"start": v(-6.03, 7.6) * mm, "end": v(-4.73, 8.47) * mm});
            skLineSegment(sketch, "E278", {"start": v(-4.73, 8.47) * mm, "end": v(-3.3, 9.13) * mm});
            skLineSegment(sketch, "E279", {"start": v(-3.3, 9.13) * mm, "end": v(-2.17, 9.47) * mm});
            skLineSegment(sketch, "E280", {"start": v(-2.17, 9.47) * mm, "end": v(-1.79, 9.55) * mm});
            skLineSegment(sketch, "E281", {"start": v(-1.79, 9.55) * mm, "end": v(-0.58, 8.28) * mm});
            skLineSegment(sketch, "E282", {"start": v(-0.58, 8.28) * mm, "end": v(-0.53, 8.23) * mm});
            skLineSegment(sketch, "E283", {"start": v(-0.53, 8.23) * mm, "end": v(-0.35, 8.12) * mm});
            skLineSegment(sketch, "E284", {"start": v(-0.35, 8.12) * mm, "end": v(-0.08, 8.06) * mm});
            skLineSegment(sketch, "E285", {"start": v(-0.08, 8.06) * mm, "end": v(0.19, 8.1) * mm});
            skLineSegment(sketch, "E286", {"start": v(0.19, 8.1) * mm, "end": v(0.38, 8.21) * mm});
            skLineSegment(sketch, "E287", {"start": v(0.38, 8.21) * mm, "end": v(0.43, 8.26) * mm});
            skLineSegment(sketch, "E288", {"start": v(0.43, 8.26) * mm, "end": v(1.77, 9.55) * mm});
            skLineSegment(sketch, "E289", {"start": v(1.77, 9.55) * mm, "end": v(2.29, 9.45) * mm});
            skLineSegment(sketch, "E290", {"start": v(2.29, 9.45) * mm, "end": v(3.78, 8.94) * mm});
            skLineSegment(sketch, "E291", {"start": v(3.78, 8.94) * mm, "end": v(5.59, 7.93) * mm});
            skLineSegment(sketch, "E292", {"start": v(5.59, 7.93) * mm, "end": v(7.13, 6.55) * mm});
            skLineSegment(sketch, "E293", {"start": v(7.13, 6.55) * mm, "end": v(8.1, 5.3) * mm});
            skLineSegment(sketch, "E294", {"start": v(8.1, 5.3) * mm, "end": v(8.36, 4.85) * mm});
            skLineSegment(sketch, "E295", {"start": v(8.36, 4.85) * mm, "end": v(7.44, 2.77) * mm});
            skLineSegment(sketch, "E296", {"start": v(7.44, 2.77) * mm, "end": v(7.41, 2.7) * mm});
            skLineSegment(sketch, "E297", {"start": v(7.41, 2.7) * mm, "end": v(7.38, 2.5) * mm});
            skLineSegment(sketch, "E298", {"start": v(7.38, 2.5) * mm, "end": v(7.43, 2.22) * mm});
            skLineSegment(sketch, "E299", {"start": v(7.43, 2.22) * mm, "end": v(7.57, 2) * mm});
            skLineSegment(sketch, "E300", {"start": v(7.57, 2) * mm, "end": v(7.74, 1.86) * mm});
            skLineSegment(sketch, "E301", {"start": v(7.74, 1.86) * mm, "end": v(7.8, 1.83) * mm});
            skLineSegment(sketch, "E302", {"start": v(7.8, 1.83) * mm, "end": v(9.58, 1.04) * mm});
            skLineSegment(sketch, "E303", {"start": v(11.88, 1) * mm, "end": v(11.85, 1.33) * mm});
            skLineSegment(sketch, "E304", {"start": v(11.85, 1.33) * mm, "end": v(12.8, 2.21) * mm});
            skLineSegment(sketch, "E305", {"start": v(12.8, 2.21) * mm, "end": v(12.83, 2.25) * mm});
            skLineSegment(sketch, "E306", {"start": v(12.83, 2.25) * mm, "end": v(12.9, 2.38) * mm});
            skLineSegment(sketch, "E307", {"start": v(12.9, 2.38) * mm, "end": v(12.9, 2.57) * mm});
            skLineSegment(sketch, "E308", {"start": v(12.9, 2.57) * mm, "end": v(12.82, 2.74) * mm});
            skLineSegment(sketch, "E309", {"start": v(12.82, 2.74) * mm, "end": v(12.72, 2.83) * mm});
            skLineSegment(sketch, "E310", {"start": v(12.72, 2.83) * mm, "end": v(12.67, 2.85) * mm});
            skLineSegment(sketch, "E311", {"start": v(12.67, 2.85) * mm, "end": v(11.46, 3.3) * mm});
            skLineSegment(sketch, "E312", {"start": v(11.46, 3.3) * mm, "end": v(11.36, 3.62) * mm});
            skLineSegment(sketch, "E313", {"start": v(11.36, 3.62) * mm, "end": v(12.12, 4.67) * mm});
            skLineSegment(sketch, "E314", {"start": v(12.12, 4.67) * mm, "end": v(12.15, 4.7) * mm});
            skLineSegment(sketch, "E315", {"start": v(12.15, 4.7) * mm, "end": v(12.18, 4.85) * mm});
            skLineSegment(sketch, "E316", {"start": v(12.18, 4.85) * mm, "end": v(12.15, 5.03) * mm});
            skLineSegment(sketch, "E317", {"start": v(12.15, 5.03) * mm, "end": v(12.04, 5.19) * mm});
            skLineSegment(sketch, "E318", {"start": v(12.04, 5.19) * mm, "end": v(11.92, 5.26) * mm});
            skLineSegment(sketch, "E319", {"start": v(11.92, 5.26) * mm, "end": v(11.87, 5.27) * mm});
            skLineSegment(sketch, "E320", {"start": v(11.87, 5.27) * mm, "end": v(10.6, 5.48) * mm});
            skLineSegment(sketch, "E321", {"start": v(10.6, 5.48) * mm, "end": v(10.44, 5.76) * mm});
            skLineSegment(sketch, "E322", {"start": v(10.44, 5.76) * mm, "end": v(10.98, 6.94) * mm});
            skLineSegment(sketch, "E323", {"start": v(10.98, 6.94) * mm, "end": v(11, 6.99) * mm});
            skLineSegment(sketch, "E324", {"start": v(11, 6.99) * mm, "end": v(11, 7.13) * mm});
            skLineSegment(sketch, "E325", {"start": v(11, 7.13) * mm, "end": v(10.94, 7.3) * mm});
            skLineSegment(sketch, "E326", {"start": v(10.94, 7.3) * mm, "end": v(10.8, 7.44) * mm});
            skLineSegment(sketch, "E327", {"start": v(10.8, 7.44) * mm, "end": v(10.66, 7.48) * mm});
            skLineSegment(sketch, "E328", {"start": v(10.66, 7.48) * mm, "end": v(10.62, 7.48) * mm});
            skLineSegment(sketch, "E329", {"start": v(10.62, 7.48) * mm, "end": v(9.32, 7.44) * mm});
            skLineSegment(sketch, "E330", {"start": v(9.32, 7.44) * mm, "end": v(9.11, 7.69) * mm});
            skLineSegment(sketch, "E331", {"start": v(9.11, 7.69) * mm, "end": v(9.41, 8.95) * mm});
            skLineSegment(sketch, "E332", {"start": v(9.41, 8.95) * mm, "end": v(9.42, 9) * mm});
            skLineSegment(sketch, "E333", {"start": v(9.42, 9) * mm, "end": v(9.4, 9.14) * mm});
            skLineSegment(sketch, "E334", {"start": v(9.4, 9.14) * mm, "end": v(9.3, 9.3) * mm});
            skLineSegment(sketch, "E335", {"start": v(9.3, 9.3) * mm, "end": v(9.14, 9.4) * mm});
            skLineSegment(sketch, "E336", {"start": v(9.14, 9.4) * mm, "end": v(9, 9.42) * mm});
            skLineSegment(sketch, "E337", {"start": v(9, 9.42) * mm, "end": v(8.95, 9.41) * mm});
            skLineSegment(sketch, "E338", {"start": v(8.95, 9.41) * mm, "end": v(7.69, 9.11) * mm});
            skLineSegment(sketch, "E339", {"start": v(7.69, 9.11) * mm, "end": v(7.44, 9.32) * mm});
            skLineSegment(sketch, "E340", {"start": v(7.44, 9.32) * mm, "end": v(7.48, 10.62) * mm});
            skLineSegment(sketch, "E341", {"start": v(7.48, 10.62) * mm, "end": v(7.49, 10.66) * mm});
            skLineSegment(sketch, "E342", {"start": v(7.49, 10.66) * mm, "end": v(7.44, 10.8) * mm});
            skLineSegment(sketch, "E343", {"start": v(7.44, 10.8) * mm, "end": v(7.3, 10.94) * mm});
            skLineSegment(sketch, "E344", {"start": v(7.3, 10.94) * mm, "end": v(7.13, 11) * mm});
            skLineSegment(sketch, "E345", {"start": v(7.13, 11) * mm, "end": v(6.99, 11) * mm});
            skLineSegment(sketch, "E346", {"start": v(6.99, 11) * mm, "end": v(6.95, 10.98) * mm});
            skLineSegment(sketch, "E347", {"start": v(6.95, 10.98) * mm, "end": v(5.77, 10.44) * mm});
            skLineSegment(sketch, "E348", {"start": v(5.77, 10.44) * mm, "end": v(5.48, 10.6) * mm});
            skLineSegment(sketch, "E349", {"start": v(5.48, 10.6) * mm, "end": v(5.27, 11.87) * mm});
            skLineSegment(sketch, "E350", {"start": v(5.27, 11.87) * mm, "end": v(5.26, 11.92) * mm});
            skLineSegment(sketch, "E351", {"start": v(5.26, 11.92) * mm, "end": v(5.19, 12.04) * mm});
            skLineSegment(sketch, "E352", {"start": v(5.19, 12.04) * mm, "end": v(5.03, 12.15) * mm});
            skLineSegment(sketch, "E353", {"start": v(5.03, 12.15) * mm, "end": v(4.85, 12.18) * mm});
            skLineSegment(sketch, "E354", {"start": v(4.85, 12.18) * mm, "end": v(4.7, 12.15) * mm});
            skLineSegment(sketch, "E355", {"start": v(4.7, 12.15) * mm, "end": v(4.67, 12.12) * mm});
            skLineSegment(sketch, "E356", {"start": v(4.67, 12.12) * mm, "end": v(3.62, 11.36) * mm});
            skLineSegment(sketch, "E357", {"start": v(3.62, 11.36) * mm, "end": v(3.3, 11.46) * mm});
            skLineSegment(sketch, "E358", {"start": v(3.3, 11.46) * mm, "end": v(2.85, 12.67) * mm});
            skLineSegment(sketch, "E359", {"start": v(2.85, 12.67) * mm, "end": v(2.84, 12.72) * mm});
            skLineSegment(sketch, "E360", {"start": v(2.84, 12.72) * mm, "end": v(2.74, 12.82) * mm});
            skLineSegment(sketch, "E361", {"start": v(2.74, 12.82) * mm, "end": v(2.57, 12.9) * mm});
            skLineSegment(sketch, "E362", {"start": v(2.57, 12.9) * mm, "end": v(2.38, 12.9) * mm});
            skLineSegment(sketch, "E363", {"start": v(2.38, 12.9) * mm, "end": v(2.25, 12.83) * mm});
            skLineSegment(sketch, "E364", {"start": v(2.25, 12.83) * mm, "end": v(2.22, 12.8) * mm});
            skLineSegment(sketch, "E365", {"start": v(2.22, 12.8) * mm, "end": v(1.33, 11.85) * mm});
            skLineSegment(sketch, "E366", {"start": v(1.33, 11.85) * mm, "end": v(1, 11.88) * mm});
            skLineSegment(sketch, "E367", {"start": v(1, 11.88) * mm, "end": v(0.32, 12.99) * mm});
            skLineSegment(sketch, "E368", {"start": v(0.32, 12.99) * mm, "end": v(0.3, 13.02) * mm});
            skLineSegment(sketch, "E369", {"start": v(0.3, 13.02) * mm, "end": v(0.18, 13.11) * mm});
            skLineSegment(sketch, "E370", {"start": v(0.18, 13.11) * mm, "end": v(0, 13.15) * mm});
            skLineSegment(sketch, "E371", {"start": v(0, 13.15) * mm, "end": v(-0.18, 13.11) * mm});
            skLineSegment(sketch, "E372", {"start": v(-0.18, 13.11) * mm, "end": v(-0.3, 13.02) * mm});
            skLineSegment(sketch, "E373", {"start": v(-0.3, 13.02) * mm, "end": v(-0.32, 12.99) * mm});
            skLineSegment(sketch, "E374", {"start": v(-0.32, 12.99) * mm, "end": v(-1, 11.88) * mm});
            skLineSegment(sketch, "E375", {"start": v(-1, 11.88) * mm, "end": v(-1.33, 11.85) * mm});
            skLineSegment(sketch, "E376", {"start": v(-1.33, 11.85) * mm, "end": v(-2.22, 12.8) * mm});
            skLineSegment(sketch, "E377", {"start": v(-2.22, 12.8) * mm, "end": v(-2.25, 12.83) * mm});
            skLineSegment(sketch, "E378", {"start": v(-2.25, 12.83) * mm, "end": v(-2.38, 12.9) * mm});
            skLineSegment(sketch, "E379", {"start": v(-2.38, 12.9) * mm, "end": v(-2.57, 12.9) * mm});
            skLineSegment(sketch, "E380", {"start": v(-2.57, 12.9) * mm, "end": v(-2.74, 12.82) * mm});
            skLineSegment(sketch, "E381", {"start": v(-2.74, 12.82) * mm, "end": v(-2.83, 12.72) * mm});
            skLineSegment(sketch, "E382", {"start": v(-2.83, 12.72) * mm, "end": v(-2.85, 12.67) * mm});
            skLineSegment(sketch, "E383", {"start": v(-2.85, 12.67) * mm, "end": v(-3.3, 11.46) * mm});
            skLineSegment(sketch, "E384", {"start": v(-3.3, 11.46) * mm, "end": v(-3.62, 11.36) * mm});
            skLineSegment(sketch, "E385", {"start": v(-3.62, 11.36) * mm, "end": v(-4.67, 12.12) * mm});
            skLineSegment(sketch, "E386", {"start": v(-4.67, 12.12) * mm, "end": v(-4.7, 12.15) * mm});
            skLineSegment(sketch, "E387", {"start": v(-4.7, 12.15) * mm, "end": v(-4.85, 12.18) * mm});
            skLineSegment(sketch, "E388", {"start": v(-4.85, 12.18) * mm, "end": v(-5.03, 12.15) * mm});
            skLineSegment(sketch, "E389", {"start": v(-5.03, 12.15) * mm, "end": v(-5.19, 12.04) * mm});
            skLineSegment(sketch, "E390", {"start": v(-5.19, 12.04) * mm, "end": v(-5.26, 11.92) * mm});
            skLineSegment(sketch, "E391", {"start": v(-5.26, 11.92) * mm, "end": v(-5.27, 11.87) * mm});
            skLineSegment(sketch, "E392", {"start": v(-5.27, 11.87) * mm, "end": v(-5.48, 10.6) * mm});
            skLineSegment(sketch, "E393", {"start": v(-5.48, 10.6) * mm, "end": v(-5.76, 10.44) * mm});
            skLineSegment(sketch, "E394", {"start": v(-5.76, 10.44) * mm, "end": v(-6.95, 10.98) * mm});
            skLineSegment(sketch, "E395", {"start": v(-6.95, 10.98) * mm, "end": v(-6.99, 11) * mm});
            skLineSegment(sketch, "E396", {"start": v(-6.99, 11) * mm, "end": v(-7.13, 11) * mm});
            skLineSegment(sketch, "E397", {"start": v(-7.13, 11) * mm, "end": v(-7.3, 10.94) * mm});
            skLineSegment(sketch, "E398", {"start": v(-7.3, 10.94) * mm, "end": v(-7.44, 10.8) * mm});
            skLineSegment(sketch, "E399", {"start": v(-7.44, 10.8) * mm, "end": v(-7.49, 10.66) * mm});
            skLineSegment(sketch, "E400", {"start": v(-7.49, 10.66) * mm, "end": v(-7.48, 10.62) * mm});
            skLineSegment(sketch, "E401", {"start": v(-7.48, 10.62) * mm, "end": v(-7.44, 9.32) * mm});
            skLineSegment(sketch, "E402", {"start": v(-7.44, 9.32) * mm, "end": v(-7.69, 9.11) * mm});
            skLineSegment(sketch, "E403", {"start": v(-7.69, 9.11) * mm, "end": v(-8.95, 9.41) * mm});
            skLineSegment(sketch, "E404", {"start": v(-8.95, 9.41) * mm, "end": v(-9, 9.42) * mm});
            skLineSegment(sketch, "E405", {"start": v(-9, 9.42) * mm, "end": v(-9.14, 9.4) * mm});
            skLineSegment(sketch, "E406", {"start": v(-9.14, 9.4) * mm, "end": v(-9.3, 9.3) * mm});
            skLineSegment(sketch, "E407", {"start": v(-9.3, 9.3) * mm, "end": v(-9.4, 9.14) * mm});
            skLineSegment(sketch, "E408", {"start": v(-9.4, 9.14) * mm, "end": v(-9.42, 9) * mm});
            skLineSegment(sketch, "E409", {"start": v(-9.42, 9) * mm, "end": v(-9.41, 8.95) * mm});
            skLineSegment(sketch, "E410", {"start": v(-9.41, 8.95) * mm, "end": v(-9.11, 7.69) * mm});
            skLineSegment(sketch, "E411", {"start": v(-9.11, 7.69) * mm, "end": v(-9.32, 7.44) * mm});
            skLineSegment(sketch, "E412", {"start": v(-9.32, 7.44) * mm, "end": v(-10.62, 7.48) * mm});
            skLineSegment(sketch, "E413", {"start": v(-10.62, 7.48) * mm, "end": v(-10.66, 7.48) * mm});
            skLineSegment(sketch, "E414", {"start": v(-10.66, 7.48) * mm, "end": v(-10.8, 7.44) * mm});
            skLineSegment(sketch, "E415", {"start": v(-10.8, 7.44) * mm, "end": v(-10.94, 7.3) * mm});
            skLineSegment(sketch, "E416", {"start": v(-10.94, 7.3) * mm, "end": v(-11, 7.13) * mm});
            skLineSegment(sketch, "E417", {"start": v(-11, 7.13) * mm, "end": v(-11, 6.99) * mm});
            skLineSegment(sketch, "E418", {"start": v(-11, 6.99) * mm, "end": v(-10.98, 6.94) * mm});
            skLineSegment(sketch, "E419", {"start": v(-10.98, 6.94) * mm, "end": v(-10.44, 5.76) * mm});
            skLineSegment(sketch, "E420", {"start": v(-10.44, 5.76) * mm, "end": v(-10.6, 5.48) * mm});
            skLineSegment(sketch, "E421", {"start": v(-10.6, 5.48) * mm, "end": v(-11.87, 5.27) * mm});
            skLineSegment(sketch, "E422", {"start": v(-11.87, 5.27) * mm, "end": v(-11.92, 5.26) * mm});
            skLineSegment(sketch, "E423", {"start": v(-11.92, 5.26) * mm, "end": v(-12.04, 5.19) * mm});
            skLineSegment(sketch, "E424", {"start": v(-12.04, 5.19) * mm, "end": v(-12.15, 5.03) * mm});
            skLineSegment(sketch, "E425", {"start": v(-12.15, 5.03) * mm, "end": v(-12.18, 4.85) * mm});
            skLineSegment(sketch, "E426", {"start": v(-12.18, 4.85) * mm, "end": v(-12.15, 4.7) * mm});
            skLineSegment(sketch, "E427", {"start": v(-12.15, 4.7) * mm, "end": v(-12.12, 4.67) * mm});
            skLineSegment(sketch, "E428", {"start": v(-12.12, 4.67) * mm, "end": v(-11.36, 3.62) * mm});
            skLineSegment(sketch, "E429", {"start": v(-11.36, 3.62) * mm, "end": v(-11.46, 3.3) * mm});
            skLineSegment(sketch, "E430", {"start": v(-11.46, 3.3) * mm, "end": v(-12.67, 2.85) * mm});
            skLineSegment(sketch, "E431", {"start": v(-12.67, 2.85) * mm, "end": v(-12.72, 2.83) * mm});
            skLineSegment(sketch, "E432", {"start": v(-12.72, 2.83) * mm, "end": v(-12.82, 2.74) * mm});
            skLineSegment(sketch, "E433", {"start": v(-12.82, 2.74) * mm, "end": v(-12.9, 2.57) * mm});
            skLineSegment(sketch, "E434", {"start": v(-12.9, 2.57) * mm, "end": v(-12.9, 2.38) * mm});
            skLineSegment(sketch, "E435", {"start": v(-12.9, 2.38) * mm, "end": v(-12.83, 2.25) * mm});
            skLineSegment(sketch, "E436", {"start": v(-12.83, 2.25) * mm, "end": v(-12.8, 2.21) * mm});
            skLineSegment(sketch, "E437", {"start": v(-12.8, 2.21) * mm, "end": v(-11.85, 1.33) * mm});
            skLineSegment(sketch, "E438", {"start": v(-11.85, 1.33) * mm, "end": v(-11.88, 1) * mm});
            skLineSegment(sketch, "E439", {"start": v(-11.88, 1) * mm, "end": v(-12.99, 0.32) * mm});
            skLineSegment(sketch, "E440", {"start": v(-12.99, 0.32) * mm, "end": v(-13.02, 0.3) * mm});
            skLineSegment(sketch, "E441", {"start": v(-13.02, 0.3) * mm, "end": v(-13.11, 0.18) * mm});
            skLineSegment(sketch, "E442", {"start": v(-13.11, 0.18) * mm, "end": v(-13.15, 0) * mm});
            skLineSegment(sketch, "E443", {"start": v(-13.15, 0) * mm, "end": v(-13.11, -0.18) * mm});
            skLineSegment(sketch, "E444", {"start": v(-13.11, -0.18) * mm, "end": v(-13.02, -0.3) * mm});
            skLineSegment(sketch, "E445", {"start": v(-13.02, -0.3) * mm, "end": v(-12.99, -0.32) * mm});
            skLineSegment(sketch, "E446", {"start": v(-12.99, -0.32) * mm, "end": v(-11.88, -1) * mm});
            skLineSegment(sketch, "E447", {"start": v(-11.88, -1) * mm, "end": v(-11.85, -1.33) * mm});
            skLineSegment(sketch, "E448", {"start": v(-11.85, -1.33) * mm, "end": v(-12.8, -2.22) * mm});
            skLineSegment(sketch, "E449", {"start": v(-12.8, -2.22) * mm, "end": v(-12.83, -2.25) * mm});
            skLineSegment(sketch, "E450", {"start": v(-12.83, -2.25) * mm, "end": v(-12.9, -2.38) * mm});
            skLineSegment(sketch, "E451", {"start": v(-12.9, -2.38) * mm, "end": v(-12.9, -2.57) * mm});
            skLineSegment(sketch, "E452", {"start": v(-12.9, -2.57) * mm, "end": v(-12.82, -2.74) * mm});
            skLineSegment(sketch, "E453", {"start": v(-12.82, -2.74) * mm, "end": v(-12.72, -2.84) * mm});
            skLineSegment(sketch, "E454", {"start": v(-12.72, -2.84) * mm, "end": v(-12.67, -2.85) * mm});
            skLineSegment(sketch, "E455", {"start": v(-12.67, -2.85) * mm, "end": v(-11.46, -3.3) * mm});
            skLineSegment(sketch, "E456", {"start": v(-11.46, -3.3) * mm, "end": v(-11.36, -3.62) * mm});
            skLineSegment(sketch, "E457", {"start": v(-11.36, -3.62) * mm, "end": v(-12.12, -4.67) * mm});
            skLineSegment(sketch, "E458", {"start": v(-12.12, -4.67) * mm, "end": v(-12.15, -4.7) * mm});
            skLineSegment(sketch, "E459", {"start": v(-12.15, -4.7) * mm, "end": v(-12.18, -4.85) * mm});
            skLineSegment(sketch, "E460", {"start": v(-12.18, -4.85) * mm, "end": v(-12.15, -5.04) * mm});
            skLineSegment(sketch, "E461", {"start": v(-12.15, -5.04) * mm, "end": v(-12.04, -5.19) * mm});
            skLineSegment(sketch, "E462", {"start": v(-12.04, -5.19) * mm, "end": v(-11.92, -5.26) * mm});
            skLineSegment(sketch, "E463", {"start": v(-11.92, -5.26) * mm, "end": v(-11.87, -5.27) * mm});
            skLineSegment(sketch, "E464", {"start": v(-11.87, -5.27) * mm, "end": v(-10.6, -5.48) * mm});
            skLineSegment(sketch, "E465", {"start": v(-10.6, -5.48) * mm, "end": v(-10.44, -5.77) * mm});
            skLineSegment(sketch, "E466", {"start": v(-10.44, -5.77) * mm, "end": v(-10.98, -6.95) * mm});
            skLineSegment(sketch, "E467", {"start": v(-10.98, -6.95) * mm, "end": v(-11, -6.99) * mm});
            skLineSegment(sketch, "E468", {"start": v(-11, -6.99) * mm, "end": v(-11, -7.13) * mm});
            skLineSegment(sketch, "E469", {"start": v(-11, -7.13) * mm, "end": v(-10.94, -7.3) * mm});
            skLineSegment(sketch, "E470", {"start": v(-10.94, -7.3) * mm, "end": v(-10.8, -7.44) * mm});
            skLineSegment(sketch, "E471", {"start": v(-10.8, -7.44) * mm, "end": v(-10.66, -7.49) * mm});
            skLineSegment(sketch, "E472", {"start": v(-10.66, -7.49) * mm, "end": v(-10.62, -7.48) * mm});
            skLineSegment(sketch, "E473", {"start": v(-10.62, -7.48) * mm, "end": v(-9.32, -7.44) * mm});
            skLineSegment(sketch, "E474", {"start": v(-9.32, -7.44) * mm, "end": v(-9.11, -7.69) * mm});
            skLineSegment(sketch, "E475", {"start": v(-9.11, -7.69) * mm, "end": v(-9.41, -8.96) * mm});
            skLineSegment(sketch, "E476", {"start": v(-9.41, -8.96) * mm, "end": v(-9.42, -9) * mm});
            skLineSegment(sketch, "E477", {"start": v(-9.42, -9) * mm, "end": v(-9.4, -9.14) * mm});
            skLineSegment(sketch, "E478", {"start": v(-9.4, -9.14) * mm, "end": v(-9.3, -9.3) * mm});
            skLineSegment(sketch, "E479", {"start": v(-9.3, -9.3) * mm, "end": v(-9.14, -9.4) * mm});
            skLineSegment(sketch, "E480", {"start": v(-9.14, -9.4) * mm, "end": v(-9, -9.42) * mm});
            skLineSegment(sketch, "E481", {"start": v(-9, -9.42) * mm, "end": v(-8.95, -9.41) * mm});
            skLineSegment(sketch, "E482", {"start": v(-8.95, -9.41) * mm, "end": v(-7.69, -9.11) * mm});
            skLineSegment(sketch, "E483", {"start": v(-7.69, -9.11) * mm, "end": v(-7.44, -9.32) * mm});
            skLineSegment(sketch, "E484", {"start": v(-7.44, -9.32) * mm, "end": v(-7.48, -10.62) * mm});
            skLineSegment(sketch, "E485", {"start": v(-7.48, -10.62) * mm, "end": v(-7.49, -10.66) * mm});
            skLineSegment(sketch, "E486", {"start": v(-7.49, -10.66) * mm, "end": v(-7.44, -10.8) * mm});
            skLineSegment(sketch, "E487", {"start": v(-7.44, -10.8) * mm, "end": v(-7.3, -10.94) * mm});
            skLineSegment(sketch, "E488", {"start": v(-7.3, -10.94) * mm, "end": v(-7.13, -11) * mm});
            skLineSegment(sketch, "E489", {"start": v(-7.13, -11) * mm, "end": v(-6.99, -11) * mm});
            skLineSegment(sketch, "E490", {"start": v(-6.99, -11) * mm, "end": v(-6.95, -10.98) * mm});
            skLineSegment(sketch, "E491", {"start": v(-6.95, -10.98) * mm, "end": v(-5.76, -10.44) * mm});
            skLineSegment(sketch, "E492", {"start": v(-5.76, -10.44) * mm, "end": v(-5.48, -10.6) * mm});
            skLineSegment(sketch, "E493", {"start": v(-5.48, -10.6) * mm, "end": v(-5.27, -11.87) * mm});
            skLineSegment(sketch, "E494", {"start": v(-5.27, -11.87) * mm, "end": v(-5.26, -11.92) * mm});
            skLineSegment(sketch, "E495", {"start": v(-5.26, -11.92) * mm, "end": v(-5.19, -12.04) * mm});
            skLineSegment(sketch, "E496", {"start": v(-5.19, -12.04) * mm, "end": v(-5.03, -12.15) * mm});
            skLineSegment(sketch, "E497", {"start": v(-5.03, -12.15) * mm, "end": v(-4.85, -12.18) * mm});
            skLineSegment(sketch, "E498", {"start": v(-4.85, -12.18) * mm, "end": v(-4.7, -12.15) * mm});
            skLineSegment(sketch, "E499", {"start": v(-4.7, -12.15) * mm, "end": v(-4.67, -12.12) * mm});
            skLineSegment(sketch, "E500", {"start": v(-4.67, -12.12) * mm, "end": v(-3.62, -11.36) * mm});
            skLineSegment(sketch, "E501", {"start": v(-3.62, -11.36) * mm, "end": v(-3.3, -11.46) * mm});
            skLineSegment(sketch, "E502", {"start": v(-3.3, -11.46) * mm, "end": v(-2.85, -12.67) * mm});
            skLineSegment(sketch, "E503", {"start": v(-2.85, -12.67) * mm, "end": v(-2.83, -12.72) * mm});
            skLineSegment(sketch, "E504", {"start": v(-2.83, -12.72) * mm, "end": v(-2.74, -12.82) * mm});
            skLineSegment(sketch, "E505", {"start": v(-2.74, -12.82) * mm, "end": v(-2.57, -12.9) * mm});
            skLineSegment(sketch, "E506", {"start": v(-2.57, -12.9) * mm, "end": v(-2.38, -12.9) * mm});
            skLineSegment(sketch, "E507", {"start": v(-2.38, -12.9) * mm, "end": v(-2.25, -12.83) * mm});
            skLineSegment(sketch, "E508", {"start": v(-2.25, -12.83) * mm, "end": v(-2.22, -12.8) * mm});
            skLineSegment(sketch, "E509", {"start": v(-2.22, -12.8) * mm, "end": v(-1.33, -11.85) * mm});
            skLineSegment(sketch, "E510", {"start": v(-1.33, -11.85) * mm, "end": v(-1, -11.88) * mm});
            skLineSegment(sketch, "E511", {"start": v(-1, -11.88) * mm, "end": v(-0.32, -12.99) * mm});
            skLineSegment(sketch, "E512", {"start": v(-0.32, -12.99) * mm, "end": v(-0.3, -13.03) * mm});
            skLineSegment(sketch, "E513", {"start": v(-0.3, -13.03) * mm, "end": v(-0.18, -13.11) * mm});
            skLineSegment(sketch, "E514", {"start": v(-0.18, -13.11) * mm, "end": v(0, -13.15) * mm});
            skLineSegment(sketch, "E515", {"start": v(0, -13.15) * mm, "end": v(0.18, -13.11) * mm});
            skLineSegment(sketch, "E516", {"start": v(0.18, -13.11) * mm, "end": v(0.3, -13.03) * mm});
            skLineSegment(sketch, "E517", {"start": v(0.3, -13.03) * mm, "end": v(0.32, -12.99) * mm});
            skLineSegment(sketch, "E518", {"start": v(0.32, -12.99) * mm, "end": v(1, -11.88) * mm});
            skLineSegment(sketch, "E519", {"start": v(1, -11.88) * mm, "end": v(1.33, -11.85) * mm});
            skLineSegment(sketch, "E520", {"start": v(1.33, -11.85) * mm, "end": v(2.22, -12.8) * mm});
            skLineSegment(sketch, "E521", {"start": v(2.22, -12.8) * mm, "end": v(2.25, -12.83) * mm});
            skLineSegment(sketch, "E522", {"start": v(2.25, -12.83) * mm, "end": v(2.38, -12.9) * mm});
            skLineSegment(sketch, "E523", {"start": v(2.38, -12.9) * mm, "end": v(2.57, -12.9) * mm});
            skLineSegment(sketch, "E524", {"start": v(2.57, -12.9) * mm, "end": v(2.74, -12.82) * mm});
            skLineSegment(sketch, "E525", {"start": v(2.74, -12.82) * mm, "end": v(2.84, -12.72) * mm});
            skLineSegment(sketch, "E526", {"start": v(2.84, -12.72) * mm, "end": v(2.85, -12.67) * mm});
            skLineSegment(sketch, "E527", {"start": v(2.85, -12.67) * mm, "end": v(3.3, -11.46) * mm});
            skLineSegment(sketch, "E528", {"start": v(3.3, -11.46) * mm, "end": v(3.62, -11.36) * mm});
            skLineSegment(sketch, "E529", {"start": v(3.62, -11.36) * mm, "end": v(4.67, -12.12) * mm});
            skLineSegment(sketch, "E530", {"start": v(4.67, -12.12) * mm, "end": v(4.7, -12.15) * mm});
            skLineSegment(sketch, "E531", {"start": v(4.7, -12.15) * mm, "end": v(4.85, -12.18) * mm});
            skLineSegment(sketch, "E532", {"start": v(4.85, -12.18) * mm, "end": v(5.03, -12.15) * mm});
            skLineSegment(sketch, "E533", {"start": v(5.03, -12.15) * mm, "end": v(5.19, -12.04) * mm});
            skLineSegment(sketch, "E534", {"start": v(5.19, -12.04) * mm, "end": v(5.26, -11.92) * mm});
            skLineSegment(sketch, "E535", {"start": v(5.26, -11.92) * mm, "end": v(5.27, -11.87) * mm});
            skLineSegment(sketch, "E536", {"start": v(5.27, -11.87) * mm, "end": v(5.48, -10.6) * mm});
            skLineSegment(sketch, "E537", {"start": v(5.48, -10.6) * mm, "end": v(5.77, -10.44) * mm});
            skLineSegment(sketch, "E538", {"start": v(5.77, -10.44) * mm, "end": v(6.95, -10.98) * mm});
            skLineSegment(sketch, "E539", {"start": v(6.95, -10.98) * mm, "end": v(6.99, -11) * mm});
            skLineSegment(sketch, "E540", {"start": v(6.99, -11) * mm, "end": v(7.13, -11) * mm});
            skLineSegment(sketch, "E541", {"start": v(7.13, -11) * mm, "end": v(7.3, -10.94) * mm});
            skLineSegment(sketch, "E542", {"start": v(7.3, -10.94) * mm, "end": v(7.44, -10.8) * mm});
            skLineSegment(sketch, "E543", {"start": v(7.44, -10.8) * mm, "end": v(7.49, -10.66) * mm});
            skLineSegment(sketch, "E544", {"start": v(7.49, -10.66) * mm, "end": v(7.48, -10.62) * mm});
            skLineSegment(sketch, "E545", {"start": v(7.48, -10.62) * mm, "end": v(7.44, -9.32) * mm});
            skLineSegment(sketch, "E546", {"start": v(7.44, -9.32) * mm, "end": v(7.69, -9.11) * mm});
            skLineSegment(sketch, "E547", {"start": v(7.69, -9.11) * mm, "end": v(8.95, -9.41) * mm});
            skLineSegment(sketch, "E548", {"start": v(8.95, -9.41) * mm, "end": v(9, -9.42) * mm});
            skLineSegment(sketch, "E549", {"start": v(9, -9.42) * mm, "end": v(9.14, -9.4) * mm});
            skLineSegment(sketch, "E550", {"start": v(9.14, -9.4) * mm, "end": v(9.3, -9.3) * mm});
            skLineSegment(sketch, "E551", {"start": v(9.3, -9.3) * mm, "end": v(9.4, -9.14) * mm});
            skLineSegment(sketch, "E552", {"start": v(9.4, -9.14) * mm, "end": v(9.42, -9) * mm});
            skLineSegment(sketch, "E553", {"start": v(9.42, -9) * mm, "end": v(9.41, -8.96) * mm});
            skLineSegment(sketch, "E554", {"start": v(9.41, -8.96) * mm, "end": v(9.11, -7.69) * mm});
            skLineSegment(sketch, "E555", {"start": v(9.11, -7.69) * mm, "end": v(9.32, -7.44) * mm});
            skLineSegment(sketch, "E556", {"start": v(9.32, -7.44) * mm, "end": v(10.62, -7.48) * mm});
            skLineSegment(sketch, "E557", {"start": v(10.62, -7.48) * mm, "end": v(10.66, -7.49) * mm});
            skLineSegment(sketch, "E558", {"start": v(10.66, -7.49) * mm, "end": v(10.8, -7.44) * mm});
            skLineSegment(sketch, "E559", {"start": v(10.8, -7.44) * mm, "end": v(10.94, -7.3) * mm});
            skLineSegment(sketch, "E560", {"start": v(10.94, -7.3) * mm, "end": v(11, -7.13) * mm});
            skLineSegment(sketch, "E561", {"start": v(11, -7.13) * mm, "end": v(11, -6.99) * mm});
            skLineSegment(sketch, "E562", {"start": v(11, -6.99) * mm, "end": v(10.98, -6.95) * mm});
            skLineSegment(sketch, "E563", {"start": v(10.98, -6.95) * mm, "end": v(10.44, -5.77) * mm});
            skLineSegment(sketch, "E564", {"start": v(10.44, -5.77) * mm, "end": v(10.6, -5.48) * mm});
            skLineSegment(sketch, "E565", {"start": v(10.6, -5.48) * mm, "end": v(11.87, -5.27) * mm});
            skLineSegment(sketch, "E566", {"start": v(11.87, -5.27) * mm, "end": v(11.92, -5.26) * mm});
            skLineSegment(sketch, "E567", {"start": v(11.92, -5.26) * mm, "end": v(12.04, -5.19) * mm});
            skLineSegment(sketch, "E568", {"start": v(12.04, -5.19) * mm, "end": v(12.15, -5.04) * mm});
            skLineSegment(sketch, "E569", {"start": v(12.15, -5.04) * mm, "end": v(12.18, -4.85) * mm});
            skLineSegment(sketch, "E570", {"start": v(12.18, -4.85) * mm, "end": v(12.15, -4.7) * mm});
            skLineSegment(sketch, "E571", {"start": v(12.15, -4.7) * mm, "end": v(12.12, -4.67) * mm});
            skLineSegment(sketch, "E572", {"start": v(12.12, -4.67) * mm, "end": v(11.36, -3.62) * mm});
            skLineSegment(sketch, "E573", {"start": v(11.36, -3.62) * mm, "end": v(11.46, -3.3) * mm});
            skLineSegment(sketch, "E574", {"start": v(11.46, -3.3) * mm, "end": v(12.67, -2.85) * mm});
            skLineSegment(sketch, "E575", {"start": v(12.67, -2.85) * mm, "end": v(12.72, -2.84) * mm});
            skLineSegment(sketch, "E576", {"start": v(12.72, -2.84) * mm, "end": v(12.82, -2.74) * mm});
            skLineSegment(sketch, "E577", {"start": v(12.82, -2.74) * mm, "end": v(12.9, -2.57) * mm});
            skLineSegment(sketch, "E578", {"start": v(12.9, -2.57) * mm, "end": v(12.9, -2.38) * mm});
            skLineSegment(sketch, "E579", {"start": v(12.9, -2.38) * mm, "end": v(12.83, -2.25) * mm});
            skLineSegment(sketch, "E580", {"start": v(12.83, -2.25) * mm, "end": v(12.8, -2.22) * mm});
            skLineSegment(sketch, "E581", {"start": v(12.8, -2.22) * mm, "end": v(11.85, -1.33) * mm});
            skLineSegment(sketch, "E582", {"start": v(11.85, -1.33) * mm, "end": v(11.88, -1) * mm});
            skLineSegment(sketch, "E583", {"start": v(11.88, -1) * mm, "end": v(12.99, -0.32) * mm});
            skLineSegment(sketch, "E584", {"start": v(12.99, -0.32) * mm, "end": v(13.02, -0.3) * mm});
            skLineSegment(sketch, "E585", {"start": v(13.02, -0.3) * mm, "end": v(13.11, -0.18) * mm});
            skLineSegment(sketch, "E586", {"start": v(13.11, -0.18) * mm, "end": v(13.15, 0) * mm});
            skLineSegment(sketch, "E587", {"start": v(13.15, 0) * mm, "end": v(13.11, 0.18) * mm});
            skLineSegment(sketch, "E588", {"start": v(13.11, 0.18) * mm, "end": v(13.02, 0.3) * mm});
            skLineSegment(sketch, "E589", {"start": v(13.02, 0.3) * mm, "end": v(12.99, 0.32) * mm});
            skLineSegment(sketch, "E590", {"start": v(12.99, 0.32) * mm, "end": v(11.88, 1) * mm});
            skSolve(sketch);
        }
        {
            var Q0;
            Q0 = qSketchRegion(id + "F9", true);
            extrude(context, id + "F10", {"entities" : qUnion([Q0]), "operationType" : NewBodyOperationType.ADD, "depth" : 1 * mm, "offsetDistance" : 25 * mm});
        }
        {
            var Q0;
            Q0=makeQuery(id+"F1.opExtrude","CAP_FACE",FACE,{"disambiguationData":[OSD([sQuery(id+"F0.wireOp",EDGE,"E0")])],"isStart":true});
            var sketch = newSketch(context, id + "F11", { "sketchPlane" : qUnion([Q0])});
            skCircle(sketch, "E591.0", {"center": v(0, 0) * mm, "radius": 25 * mm});
            skCircle(sketch, "E592.0", {"center": v(0, 0) * mm, "radius": 23 * mm});
            skSolve(sketch);
        }
        {
            var Q0;
            Q0 = qSketchRegion(id + "F11", true);
            extrude(context, id + "F12", {"entities" : qUnion([Q0]), "operationType" : NewBodyOperationType.ADD, "depth" : 1.5 * mm, "offsetDistance" : 25 * mm});
        }
    });
